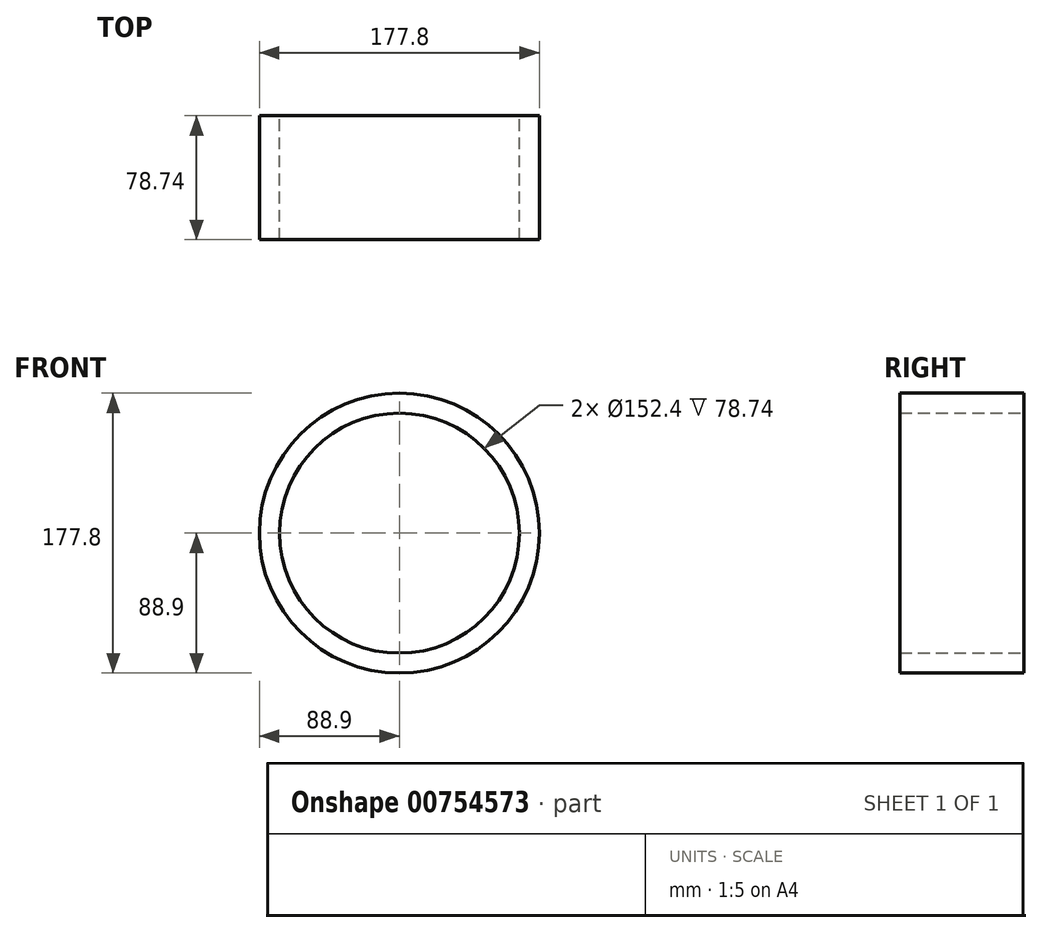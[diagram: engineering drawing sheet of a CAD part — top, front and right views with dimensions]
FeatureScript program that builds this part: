
annotation { "Feature Type Name" : "Feature", "Feature Type Description" : "" }
export const myFeature = defineFeature(function(context is Context, id is Id, definition is map)
    precondition{}
    {
        {
            var Q0;
            Q0=qCreatedBy(makeId("Front.planeOp"),FACE);
            var sketch = newSketch(context, id + "F0", { "sketchPlane" : qUnion([Q0])});
            skCircle(sketch, "E0", {"center": v(0, 0) * mm, "radius": 88.9 * mm});
            skCircle(sketch, "E1", {"center": v(0, 0) * mm, "radius": 76.2 * mm});
            skSolve(sketch);
        }
        {
            var Q0;
            Q0=makeQuery(id+"F0.imprint","IMPRINT",FACE,{"disambiguationData":[TD([[makeQuery(id+"F0.imprint","IMPRINT",EDGE,{"derivedFrom":sQuery(id+"F0.wireOp",EDGE,"E0")}),1.0]])]});
            extrude(context, id + "F1", {"entities" : qUnion([Q0]), "depth" : 78.74 * mm, "offsetDistance" : 25.4 * mm});
        }
    });
